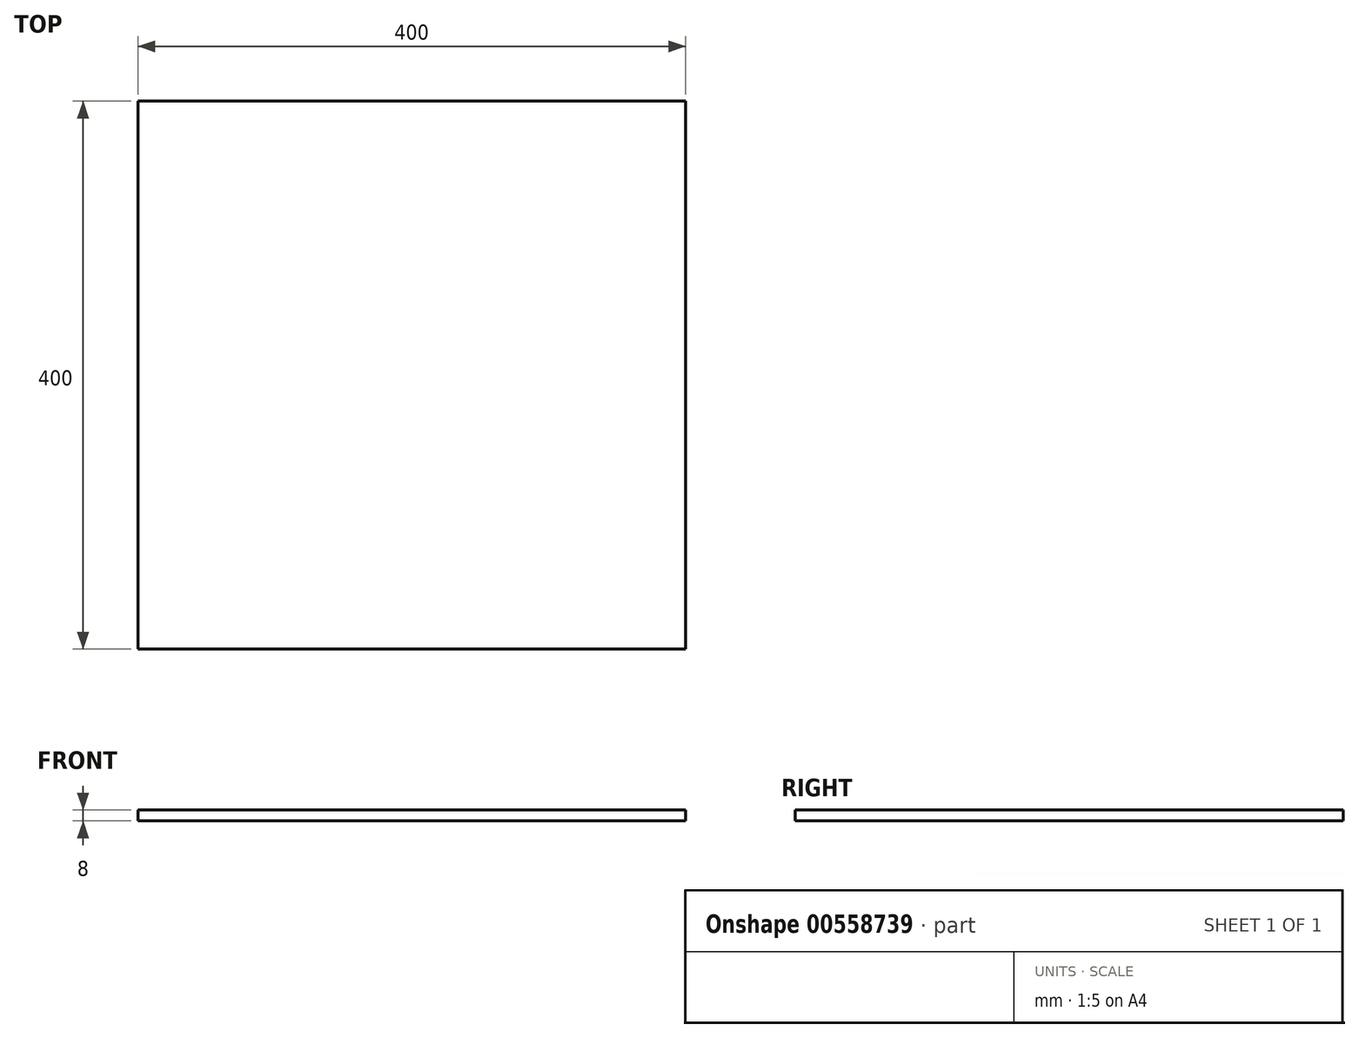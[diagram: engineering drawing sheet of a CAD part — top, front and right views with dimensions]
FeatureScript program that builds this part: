
annotation { "Feature Type Name" : "Feature", "Feature Type Description" : "" }
export const myFeature = defineFeature(function(context is Context, id is Id, definition is map)
    precondition{}
    {
        {
            var Q0;
            Q0=qCreatedBy(makeId("Top.planeOp"),FACE);
            var sketch = newSketch(context, id + "F0", { "sketchPlane" : qUnion([Q0])});
            skLineSegment(sketch, "E0.bottom", {"start": v(-197.46, 190.95) * mm, "end": v(202.54, 190.95) * mm});
            skLineSegment(sketch, "E0.top", {"start": v(-197.46, -209.05) * mm, "end": v(202.54, -209.05) * mm});
            skLineSegment(sketch, "E0.left", {"start": v(-197.46, 190.95) * mm, "end": v(-197.46, -209.05) * mm});
            skLineSegment(sketch, "E0.right", {"start": v(202.54, 190.95) * mm, "end": v(202.54, -209.05) * mm});
            skSolve(sketch);
        }
        {
            var Q0;
            Q0=makeQuery(id+"F0.imprint","IMPRINT",FACE,{"disambiguationData":[TD([[makeQuery(id+"F0.imprint","IMPRINT",EDGE,{"derivedFrom":sQuery(id+"F0.wireOp",EDGE,"E0.bottom")}),-1.0]])]});
            extrude(context, id + "F1", {"entities" : qUnion([Q0]), "depth" : 8 * mm, "offsetDistance" : 25 * mm});
        }
    });
